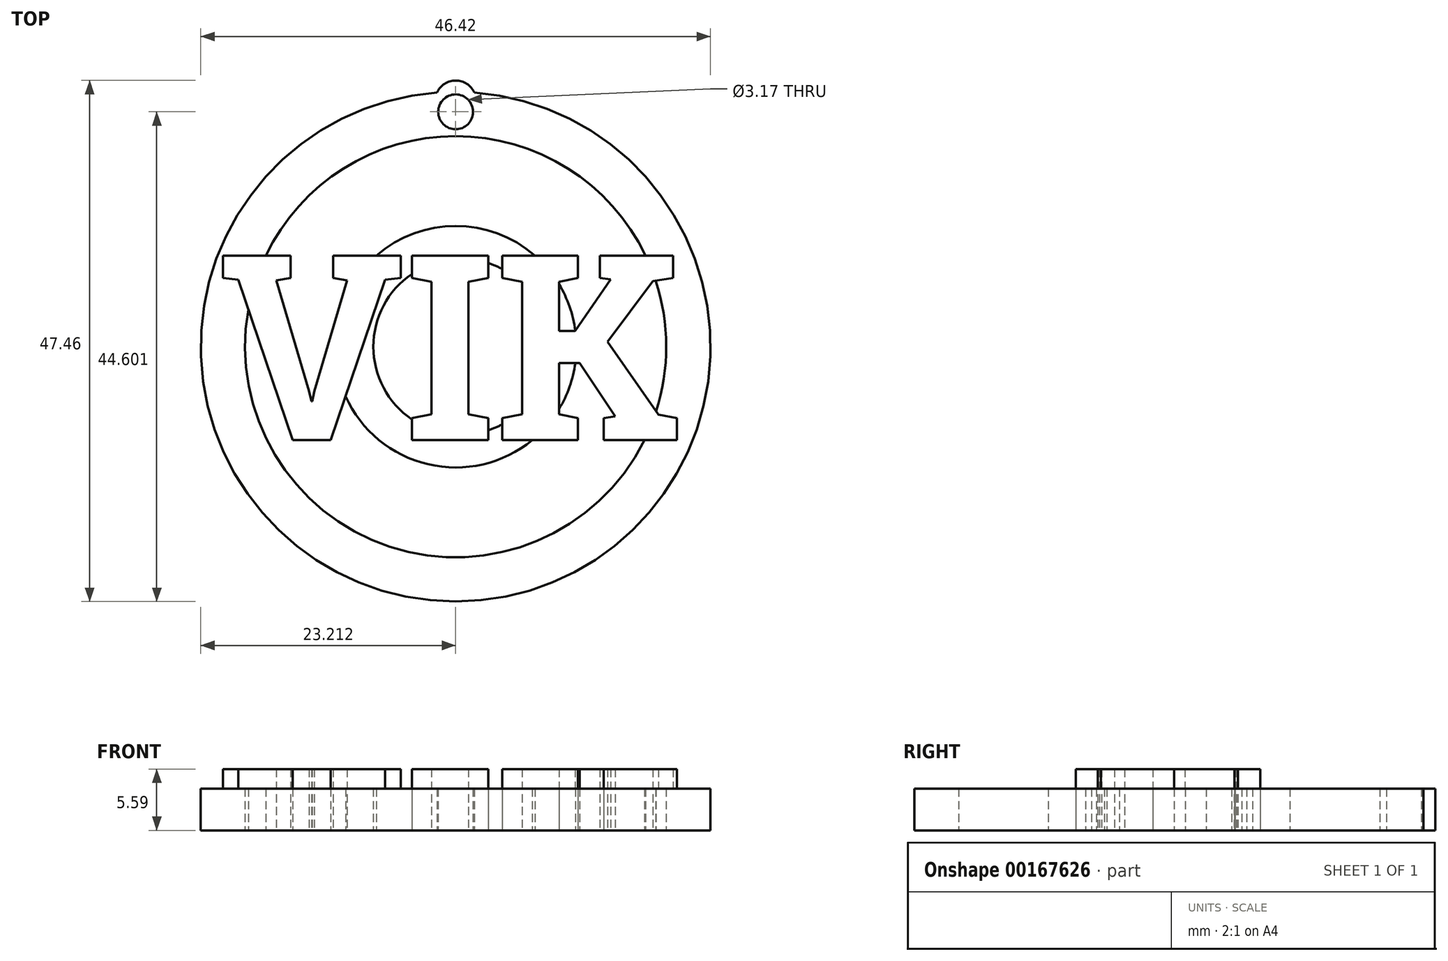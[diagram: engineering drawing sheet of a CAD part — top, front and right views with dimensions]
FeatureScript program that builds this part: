
annotation { "Feature Type Name" : "Feature", "Feature Type Description" : "" }
export const myFeature = defineFeature(function(context is Context, id is Id, definition is map)
    precondition{}
    {
        {
            var Q0;
            Q0=qCreatedBy(makeId("Top.planeOp"),FACE);
            var sketch = newSketch(context, id + "F0", { "sketchPlane" : qUnion([Q0])});
            skText(sketch, "E0", { "text": "VIK", "fontName": "RobotoSlab-Bold.ttf"});
            skArc(sketch, "E1", {"start": v(4.79, 29) * mm, "mid": v(6.48, -17.35) * mm, "end": v(8.18, 29) * mm});
            skCircle(sketch, "E2", {"center": v(6.48, 5.86) * mm, "radius": 11 * mm});
            skCircle(sketch, "E3", {"center": v(6.99, 5.86) * mm, "radius": 8 * mm});
            skCircle(sketch, "E4", {"center": v(6.48, 27.25) * mm, "radius": 1.59 * mm});
            skCircle(sketch, "E5", {"center": v(6.48, 5.86) * mm, "radius": 19.18 * mm});
            skArc(sketch, "E6", {"start": v(8.18, 29) * mm, "mid": v(6.48, 30.1) * mm, "end": v(4.79, 29) * mm});
            const initialGuessF0  = {"E0": [-0.0151, -0.00265, 1, 0, 0.01703]};
            skSetInitialGuess(sketch, initialGuessF0);
            skSolve(sketch);
        }
        {
            var Q0;
            {var subQ10=sQuery(id+"F0.wireOp",EDGE,"E0.sketch_text.stroke-6");var subQ11=sQuery(id+"F0.wireOp",EDGE,"E0.sketch_text.stroke-5");var subQ12=makeQuery(id+"F0.imprint","INTERSECT",VERTEX,{"derivedFrom":[subQ11,subQ10]});Q0=makeQuery(id+"F0.imprint","IMPRINT",FACE,{"disambiguationData":[TD([[makeQuery(id+"F0.imprint","IMPRINT",EDGE,{"disambiguationData":[TD([[subQ12,1.0]])],"derivedFrom":subQ11}),-1.0]])]});}
            var Q1;
            {var subQ0=sQuery(id+"F0.wireOp",EDGE,"E0.sketch_text.stroke-7");Q1=makeQuery(id+"F0.imprint","IMPRINT",FACE,{"disambiguationData":[TD([[makeQuery(id+"F0.imprint","IMPRINT",EDGE,{"derivedFrom":subQ0}),-1.0]])]});}
            var Q2;
            {var subQ0=sQuery(id+"F0.wireOp",EDGE,"E0.sketch_text.stroke-10");Q2=makeQuery(id+"F0.imprint","IMPRINT",FACE,{"disambiguationData":[TD([[makeQuery(id+"F0.imprint","IMPRINT",EDGE,{"derivedFrom":subQ0}),-1.0]])]});}
            var Q3;
            Q3=makeQuery(id+"F0.imprint","IMPRINT",FACE,{"disambiguationData":[TD([[makeQuery(id+"F0.imprint","IMPRINT",EDGE,{"derivedFrom":sQuery(id+"F0.wireOp",EDGE,"E0.sketch_text.stroke-0")}),-1.0]])]});
            var Q4;
            {var subQ4=sQuery(id+"F0.wireOp",EDGE,"E0.sketch_text.stroke-14");Q4=makeQuery(id+"F0.imprint","IMPRINT",FACE,{"disambiguationData":[TD([[makeQuery(id+"F0.imprint","IMPRINT",EDGE,{"derivedFrom":subQ4}),-1.0]])]});}
            var Q5;
            Q5=makeQuery(id+"F0.imprint","IMPRINT",FACE,{"disambiguationData":[TD([[makeQuery(id+"F0.imprint","IMPRINT",EDGE,{"derivedFrom":sQuery(id+"F0.wireOp",EDGE,"E0.sketch_text.stroke-18")}),-1.0]])]});
            var Q6;
            Q6=makeQuery(id+"F0.imprint","IMPRINT",FACE,{"disambiguationData":[TD([[makeQuery(id+"F0.imprint","IMPRINT",EDGE,{"derivedFrom":sQuery(id+"F0.wireOp",EDGE,"E0.sketch_text.stroke-30")}),-1.0]])]});
            var Q7;
            {var subQ1=sQuery(id+"F0.wireOp",EDGE,"E0.sketch_text.stroke-34");var subQ7=sQuery(id+"F0.wireOp",EDGE,"E3");var subQ9=makeQuery(id+"F0.imprint","INTERSECT",VERTEX,{"derivedFrom":[subQ1,subQ7]});Q7=makeQuery(id+"F0.imprint","IMPRINT",FACE,{"disambiguationData":[TD([[makeQuery(id+"F0.imprint","IMPRINT",EDGE,{"disambiguationData":[TD([[subQ9,-1.0]])],"derivedFrom":subQ1}),-1.0]])]});}
            var Q8;
            {var subQ0=sQuery(id+"F0.wireOp",EDGE,"E0.sketch_text.stroke-35");Q8=makeQuery(id+"F0.imprint","IMPRINT",FACE,{"disambiguationData":[TD([[makeQuery(id+"F0.imprint","IMPRINT",EDGE,{"derivedFrom":subQ0}),-1.0]])]});}
            var Q9;
            {var subQ7=sQuery(id+"F0.wireOp",EDGE,"E0.sketch_text.stroke-39");var subQ8=sQuery(id+"F0.wireOp",EDGE,"E0.sketch_text.stroke-38");var subQ9=makeQuery(id+"F0.imprint","INTERSECT",VERTEX,{"derivedFrom":[subQ8,subQ7]});Q9=makeQuery(id+"F0.imprint","IMPRINT",FACE,{"disambiguationData":[TD([[makeQuery(id+"F0.imprint","IMPRINT",EDGE,{"disambiguationData":[TD([[subQ9,1.0]])],"derivedFrom":subQ8}),-1.0]])]});}
            var Q10;
            {var subQ11=sQuery(id+"F0.wireOp",EDGE,"E0.sketch_text.stroke-40");Q10=makeQuery(id+"F0.imprint","IMPRINT",FACE,{"disambiguationData":[TD([[makeQuery(id+"F0.imprint","IMPRINT",EDGE,{"derivedFrom":subQ11}),-1.0]])]});}
            var Q11;
            {var subQ5=sQuery(id+"F0.wireOp",EDGE,"E0.sketch_text.stroke-55");var subQ7=sQuery(id+"F0.wireOp",EDGE,"E0.sketch_text.stroke-54");var subQ8=makeQuery(id+"F0.imprint","INTERSECT",VERTEX,{"derivedFrom":[subQ7,subQ5]});Q11=makeQuery(id+"F0.imprint","IMPRINT",FACE,{"disambiguationData":[TD([[makeQuery(id+"F0.imprint","IMPRINT",EDGE,{"disambiguationData":[TD([[subQ8,1.0]])],"derivedFrom":subQ7}),-1.0]])]});}
            var Q12;
            {var subQ0=sQuery(id+"F0.wireOp",EDGE,"E0.sketch_text.stroke-56");Q12=makeQuery(id+"F0.imprint","IMPRINT",FACE,{"disambiguationData":[TD([[makeQuery(id+"F0.imprint","IMPRINT",EDGE,{"derivedFrom":subQ0}),-1.0]])]});}
            var Q13;
            {var subQ4=sQuery(id+"F0.wireOp",EDGE,"E0.sketch_text.stroke-47");Q13=makeQuery(id+"F0.imprint","IMPRINT",FACE,{"disambiguationData":[TD([[makeQuery(id+"F0.imprint","IMPRINT",EDGE,{"derivedFrom":subQ4}),-1.0]])]});}
            var Q14;
            {var subQ0=sQuery(id+"F0.wireOp",EDGE,"E0.sketch_text.stroke-43");Q14=makeQuery(id+"F0.imprint","IMPRINT",FACE,{"disambiguationData":[TD([[makeQuery(id+"F0.imprint","IMPRINT",EDGE,{"derivedFrom":subQ0}),-1.0]])]});}
            var Q15;
            {var subQ8=sQuery(id+"F0.wireOp",EDGE,"E0.sketch_text.stroke-21");Q15=makeQuery(id+"F0.imprint","IMPRINT",FACE,{"disambiguationData":[TD([[makeQuery(id+"F0.imprint","IMPRINT",EDGE,{"derivedFrom":subQ8}),-1.0]])]});}
            var Q16;
            {var subQ0=sQuery(id+"F0.wireOp",EDGE,"E0.sketch_text.stroke-25");Q16=makeQuery(id+"F0.imprint","IMPRINT",FACE,{"disambiguationData":[TD([[makeQuery(id+"F0.imprint","IMPRINT",EDGE,{"derivedFrom":subQ0}),-1.0]])]});}
            var Q17;
            {var subQ0=sQuery(id+"F0.wireOp",EDGE,"E0.sketch_text.stroke-33");var subQ1=sQuery(id+"F0.wireOp",EDGE,"E0.sketch_text.stroke-32");var subQ2=makeQuery(id+"F0.imprint","INTERSECT",VERTEX,{"derivedFrom":[subQ1,subQ0]});Q17=makeQuery(id+"F0.imprint","IMPRINT",FACE,{"disambiguationData":[TD([[makeQuery(id+"F0.imprint","IMPRINT",EDGE,{"disambiguationData":[TD([[subQ2,1.0]])],"derivedFrom":subQ1}),-1.0]])]});}
            var Q18;
            {var subQ0=sQuery(id+"F0.wireOp",EDGE,"E3");var subQ1=sQuery(id+"F0.wireOp",EDGE,"E0.sketch_text.stroke-31");var subQ2=makeQuery(id+"F0.imprint","INTERSECT",VERTEX,{"disambiguationData":[OD(0.0)],"derivedFrom":[subQ1,subQ0]});Q18=makeQuery(id+"F0.imprint","IMPRINT",FACE,{"disambiguationData":[TD([[makeQuery(id+"F0.imprint","IMPRINT",EDGE,{"disambiguationData":[TD([[subQ2,-1.0]])],"derivedFrom":subQ1}),-1.0]])]});}
            extrude(context, id + "F1", {"entities" : qUnion([Q0, Q1, Q2, Q3, Q4, Q5, Q6, Q7, Q8, Q9, Q10, Q11, Q12, Q13, Q14, Q15, Q16, Q17, Q18]), "depth" : 5.6 * mm});
        }
        {
            var Q0;
            {var subQ14=sQuery(id+"F0.wireOp",EDGE,"E0.sketch_text.stroke-14");Q0=makeQuery(id+"F0.imprint","IMPRINT",FACE,{"disambiguationData":[TD([[makeQuery(id+"F0.imprint","IMPRINT",EDGE,{"derivedFrom":subQ14}),1.0]])]});}
            var Q1;
            {var subQ11=sQuery(id+"F0.wireOp",EDGE,"E0.sketch_text.stroke-9");Q1=makeQuery(id+"F0.imprint","IMPRINT",FACE,{"disambiguationData":[TD([[makeQuery(id+"F0.imprint","IMPRINT",EDGE,{"derivedFrom":subQ11}),1.0]])]});}
            var Q2;
            {var subQ0=sQuery(id+"F0.wireOp",EDGE,"E3");var subQ1=sQuery(id+"F0.wireOp",EDGE,"E0.sketch_text.stroke-31");var subQ2=makeQuery(id+"F0.imprint","INTERSECT",VERTEX,{"disambiguationData":[OD(0.0)],"derivedFrom":[subQ1,subQ0]});Q2=makeQuery(id+"F0.imprint","IMPRINT",FACE,{"disambiguationData":[TD([[makeQuery(id+"F0.imprint","IMPRINT",EDGE,{"disambiguationData":[TD([[subQ2,-1.0]])],"derivedFrom":subQ1}),-1.0]])]});}
            var Q3;
            {var subQ0=sQuery(id+"F0.wireOp",EDGE,"E0.sketch_text.stroke-38");Q3=makeQuery(id+"F0.imprint","IMPRINT",FACE,{"disambiguationData":[TD([[makeQuery(id+"F0.imprint","IMPRINT",EDGE,{"derivedFrom":subQ0}),1.0]])]});}
            var Q4;
            {var subQ0=sQuery(id+"F0.wireOp",EDGE,"E0.sketch_text.stroke-54");var subQ1=sQuery(id+"F0.wireOp",EDGE,"E0.sketch_text.stroke-53");var subQ2=makeQuery(id+"F0.imprint","INTERSECT",VERTEX,{"derivedFrom":[subQ1,subQ0]});Q4=makeQuery(id+"F0.imprint","IMPRINT",FACE,{"disambiguationData":[TD([[makeQuery(id+"F0.imprint","IMPRINT",EDGE,{"disambiguationData":[TD([[subQ2,1.0]])],"derivedFrom":subQ1}),1.0]])]});}
            extrude(context, id + "F2", {"entities" : qUnion([Q0, Q1, Q2, Q3, Q4]), "operationType" : NewBodyOperationType.ADD, "depth" : 3.8 * mm});
        }
    });
